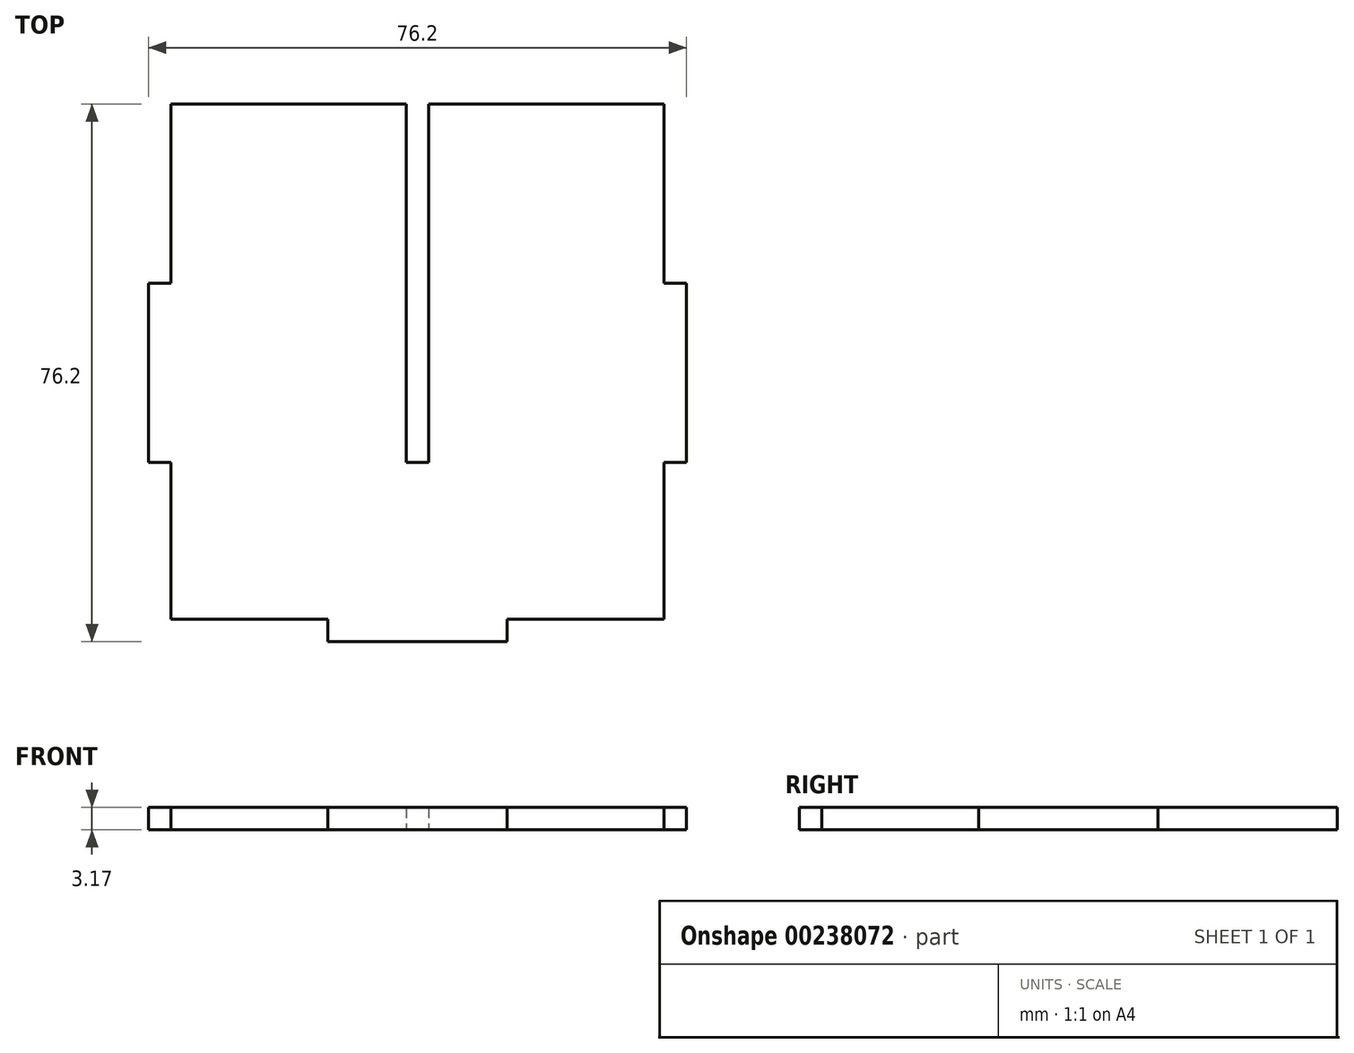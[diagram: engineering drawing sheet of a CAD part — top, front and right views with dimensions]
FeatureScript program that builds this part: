
annotation { "Feature Type Name" : "Feature", "Feature Type Description" : "" }
export const myFeature = defineFeature(function(context is Context, id is Id, definition is map)
    precondition{}
    {
        {
            var Q0;
            Q0=qCreatedBy(makeId("Top.planeOp"),FACE);
            var sketch = newSketch(context, id + "F0", { "sketchPlane" : qUnion([Q0])});
            skLineSegment(sketch, "E0.bottom", {"start": v(34.93, -25.4) * mm, "end": v(-34.93, -25.4) * mm});
            skLineSegment(sketch, "E0.top", {"start": v(34.93, -47.62) * mm, "end": v(-34.93, -47.63) * mm});
            skLineSegment(sketch, "E0.left", {"start": v(34.93, -25.4) * mm, "end": v(34.93, -47.62) * mm});
            skLineSegment(sketch, "E0.right", {"start": v(-34.93, -25.4) * mm, "end": v(-34.93, -47.62) * mm});
            skPoint(sketch, "E0.middle", {"position": v(0, -36.51) * mm});
            skLineSegment(sketch, "E1.bottom", {"start": v(12.7, -47.62) * mm, "end": v(-12.7, -47.62) * mm});
            skLineSegment(sketch, "E1.top", {"start": v(12.7, -50.8) * mm, "end": v(-12.7, -50.8) * mm});
            skLineSegment(sketch, "E1.left", {"start": v(12.7, -47.62) * mm, "end": v(12.7, -50.8) * mm});
            skLineSegment(sketch, "E1.right", {"start": v(-12.7, -47.62) * mm, "end": v(-12.7, -50.8) * mm});
            skPoint(sketch, "E1.middle", {"position": v(0, -49.21) * mm});
            skLineSegment(sketch, "E2.bottom", {"start": v(-34.93, -25.4) * mm, "end": v(-1.59, -25.4) * mm});
            skLineSegment(sketch, "E2.top", {"start": v(-34.93, 25.4) * mm, "end": v(-1.59, 25.4) * mm});
            skLineSegment(sketch, "E2.left", {"start": v(-34.93, -25.4) * mm, "end": v(-34.93, 25.4) * mm});
            skLineSegment(sketch, "E2.right", {"start": v(-1.59, -25.4) * mm, "end": v(-1.59, 25.4) * mm});
            skLineSegment(sketch, "E3.MirrorCS", {"start": v(34.93, 25.4) * mm, "end": v(1.59, 25.4) * mm});
            skLineSegment(sketch, "E4.MirrorCS", {"start": v(34.93, -25.4) * mm, "end": v(34.93, 25.4) * mm});
            skLineSegment(sketch, "E5.MirrorCS", {"start": v(1.59, -25.4) * mm, "end": v(1.59, 25.4) * mm});
            skLineSegment(sketch, "E6.MirrorCS", {"start": v(34.93, -25.4) * mm, "end": v(1.59, -25.4) * mm});
            skLineSegment(sketch, "E7.bottom", {"start": v(-34.93, -25.4) * mm, "end": v(-38.1, -25.4) * mm});
            skLineSegment(sketch, "E7.top", {"start": v(-34.93, 0) * mm, "end": v(-38.1, 0) * mm});
            skLineSegment(sketch, "E7.left", {"start": v(-34.93, -25.4) * mm, "end": v(-34.93, 0) * mm});
            skLineSegment(sketch, "E7.right", {"start": v(-38.1, -25.4) * mm, "end": v(-38.1, 0) * mm});
            skLineSegment(sketch, "E8.MirrorCS", {"start": v(38.1, -25.4) * mm, "end": v(38.1, 0) * mm});
            skLineSegment(sketch, "E9.MirrorCS", {"start": v(34.93, -25.4) * mm, "end": v(34.93, 0) * mm});
            skLineSegment(sketch, "E10.MirrorCS", {"start": v(34.93, 0) * mm, "end": v(38.1, 0) * mm});
            skLineSegment(sketch, "E11.MirrorCS", {"start": v(34.93, -25.4) * mm, "end": v(38.1, -25.4) * mm});
            skSolve(sketch);
        }
        {
            var Q0;
            Q0 = qSketchRegion(id + "F0", true);
            extrude(context, id + "F1", {"entities" : qUnion([Q0]), "depth" : 3.17 * mm});
        }
    });
